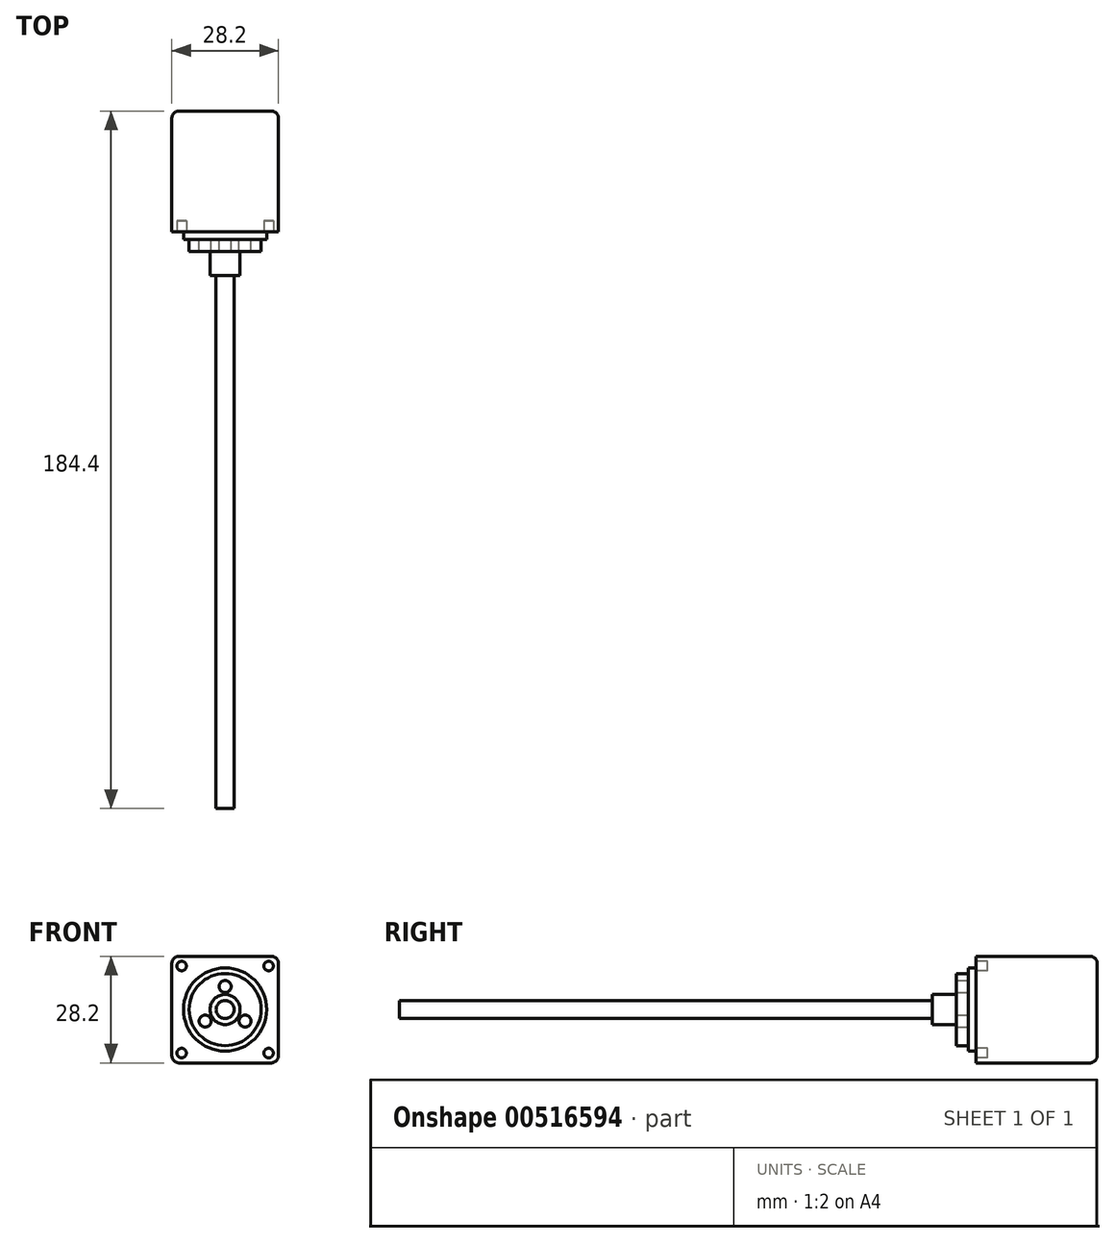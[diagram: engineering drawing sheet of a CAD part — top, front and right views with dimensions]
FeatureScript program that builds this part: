
annotation { "Feature Type Name" : "Feature", "Feature Type Description" : "" }
export const myFeature = defineFeature(function(context is Context, id is Id, definition is map)
    precondition{}
    {
        {
            var Q0;
            Q0=qCreatedBy(makeId("Front.planeOp"),FACE);
            var sketch = newSketch(context, id + "F0", { "sketchPlane" : qUnion([Q0])});
            skLineSegment(sketch, "E0.bottom", {"start": v(14.1, 14.1) * mm, "end": v(-14.1, 14.1) * mm});
            skLineSegment(sketch, "E0.top", {"start": v(14.1, -14.1) * mm, "end": v(-14.1, -14.1) * mm});
            skLineSegment(sketch, "E0.left", {"start": v(14.1, 14.1) * mm, "end": v(14.1, -14.1) * mm});
            skLineSegment(sketch, "E0.right", {"start": v(-14.1, 14.1) * mm, "end": v(-14.1, -14.1) * mm});
            skPoint(sketch, "E0.middle", {"position": v(0, 0) * mm});
            skCircle(sketch, "E1", {"center": v(0, 0) * mm, "radius": 11 * mm});
            skLineSegment(sketch, "E2.bottom", {"start": v(11.5, -11.5) * mm, "end": v(-11.5, -11.5) * mm, "construction": true});
            skLineSegment(sketch, "E2.top", {"start": v(11.5, 11.5) * mm, "end": v(-11.5, 11.5) * mm, "construction": true});
            skLineSegment(sketch, "E2.left", {"start": v(11.5, -11.5) * mm, "end": v(11.5, 11.5) * mm, "construction": true});
            skLineSegment(sketch, "E2.right", {"start": v(-11.5, -11.5) * mm, "end": v(-11.5, 11.5) * mm, "construction": true});
            skCircle(sketch, "E3", {"center": v(-11.5, 11.5) * mm, "radius": 1.25 * mm});
            skCircle(sketch, "E4", {"center": v(11.5, 11.5) * mm, "radius": 1.25 * mm});
            skCircle(sketch, "E5", {"center": v(-11.5, -11.5) * mm, "radius": 1.25 * mm});
            skCircle(sketch, "E6", {"center": v(11.5, -11.5) * mm, "radius": 1.25 * mm});
            skCircle(sketch, "E7", {"center": v(0, 0) * mm, "radius": 2.38 * mm});
            skSolve(sketch);
        }
        {
            var Q0;
            Q0=makeQuery(id+"F0.imprint","IMPRINT",FACE,{"disambiguationData":[TD([[makeQuery(id+"F0.imprint","IMPRINT",EDGE,{"derivedFrom":sQuery(id+"F0.wireOp",EDGE,"E0.bottom")}),1.0]])]});
            var Q1;
            Q1=makeQuery(id+"F0.imprint","IMPRINT",FACE,{"disambiguationData":[TD([[makeQuery(id+"F0.imprint","IMPRINT",EDGE,{"derivedFrom":sQuery(id+"F0.wireOp",EDGE,"E4")}),1.0]])]});
            var Q2;
            Q2=makeQuery(id+"F0.imprint","IMPRINT",FACE,{"disambiguationData":[TD([[makeQuery(id+"F0.imprint","IMPRINT",EDGE,{"derivedFrom":sQuery(id+"F0.wireOp",EDGE,"E6")}),1.0]])]});
            var Q3;
            Q3=makeQuery(id+"F0.imprint","IMPRINT",FACE,{"disambiguationData":[TD([[makeQuery(id+"F0.imprint","IMPRINT",EDGE,{"derivedFrom":sQuery(id+"F0.wireOp",EDGE,"E5")}),1.0]])]});
            var Q4;
            Q4=makeQuery(id+"F0.imprint","IMPRINT",FACE,{"disambiguationData":[TD([[makeQuery(id+"F0.imprint","IMPRINT",EDGE,{"derivedFrom":sQuery(id+"F0.wireOp",EDGE,"E3")}),1.0]])]});
            var Q5;
            Q5=makeQuery(id+"F0.imprint","IMPRINT",FACE,{"disambiguationData":[TD([[makeQuery(id+"F0.imprint","IMPRINT",EDGE,{"derivedFrom":sQuery(id+"F0.wireOp",EDGE,"E1")}),1.0]])]});
            var Q6;
            Q6=makeQuery(id+"F0.imprint","IMPRINT",FACE,{"disambiguationData":[TD([[makeQuery(id+"F0.imprint","IMPRINT",EDGE,{"derivedFrom":sQuery(id+"F0.wireOp",EDGE,"E7")}),1.0]])]});
            extrude(context, id + "F1", {"entities" : qUnion([Q0, Q1, Q2, Q3, Q4, Q5, Q6]), "oppositeDirection" : true, "depth" : 32 * mm, "offsetDistance" : 25 * mm});
        }
        {
            var Q0;
            Q0=makeQuery(id+"F0.imprint","IMPRINT",FACE,{"disambiguationData":[TD([[makeQuery(id+"F0.imprint","IMPRINT",EDGE,{"derivedFrom":sQuery(id+"F0.wireOp",EDGE,"E7")}),1.0]])]});
            extrude(context, id + "F2", {"entities" : qUnion([Q0]), "depth" : 152.4 * mm, "offsetDistance" : 25 * mm});
        }
        {
            var Q0;
            Q0=makeQuery(id+"F0.imprint","IMPRINT",FACE,{"disambiguationData":[TD([[makeQuery(id+"F0.imprint","IMPRINT",EDGE,{"derivedFrom":sQuery(id+"F0.wireOp",EDGE,"E1")}),1.0]])]});
            extrude(context, id + "F3", {"entities" : qUnion([Q0]), "operationType" : NewBodyOperationType.ADD, "depth" : 2 * mm, "offsetDistance" : 25 * mm});
        }
        {
            var Q0;
            Q0=makeQuery(id+"F0.imprint","IMPRINT",FACE,{"disambiguationData":[TD([[makeQuery(id+"F0.imprint","IMPRINT",EDGE,{"derivedFrom":sQuery(id+"F0.wireOp",EDGE,"E3")}),1.0]])]});
            var Q1;
            Q1=makeQuery(id+"F0.imprint","IMPRINT",FACE,{"disambiguationData":[TD([[makeQuery(id+"F0.imprint","IMPRINT",EDGE,{"derivedFrom":sQuery(id+"F0.wireOp",EDGE,"E4")}),1.0]])]});
            var Q2;
            Q2=makeQuery(id+"F0.imprint","IMPRINT",FACE,{"disambiguationData":[TD([[makeQuery(id+"F0.imprint","IMPRINT",EDGE,{"derivedFrom":sQuery(id+"F0.wireOp",EDGE,"E6")}),1.0]])]});
            var Q3;
            Q3=makeQuery(id+"F0.imprint","IMPRINT",FACE,{"disambiguationData":[TD([[makeQuery(id+"F0.imprint","IMPRINT",EDGE,{"derivedFrom":sQuery(id+"F0.wireOp",EDGE,"E5")}),1.0]])]});
            extrude(context, id + "F4", {"entities" : qUnion([Q0, Q1, Q2, Q3]), "operationType" : NewBodyOperationType.REMOVE, "oppositeDirection" : true, "depth" : 3 * mm, "offsetDistance" : 25 * mm});
        }
        {
            var Q0;
            Q0=makeQuery(id+"F1.opExtrude","SWEPT_EDGE",EDGE,{"disambiguationData":[OSD([sQuery(id+"F0.wireOp",EDGE,"E0.bottom"),sQuery(id+"F0.wireOp",EDGE,"E0.right")])]});
            var Q1;
            Q1=makeQuery(id+"F1.opExtrude","CAP_EDGE",EDGE,{"disambiguationData":[OSD([sQuery(id+"F0.wireOp",EDGE,"E0.bottom")])],"isStart":false});
            var Q2;
            Q2=makeQuery(id+"F1.opExtrude","SWEPT_EDGE",EDGE,{"disambiguationData":[OSD([sQuery(id+"F0.wireOp",EDGE,"E0.bottom"),sQuery(id+"F0.wireOp",EDGE,"E0.left")])]});
            var Q3;
            Q3=makeQuery(id+"F1.opExtrude","CAP_EDGE",EDGE,{"disambiguationData":[OSD([sQuery(id+"F0.wireOp",EDGE,"E0.left")])],"isStart":false});
            var Q4;
            Q4=makeQuery(id+"F1.opExtrude","SWEPT_EDGE",EDGE,{"disambiguationData":[OSD([sQuery(id+"F0.wireOp",EDGE,"E0.top"),sQuery(id+"F0.wireOp",EDGE,"E0.left")])]});
            var Q5;
            Q5=makeQuery(id+"F1.opExtrude","CAP_EDGE",EDGE,{"disambiguationData":[OSD([sQuery(id+"F0.wireOp",EDGE,"E0.top")])],"isStart":false});
            var Q6;
            Q6=makeQuery(id+"F1.opExtrude","SWEPT_EDGE",EDGE,{"disambiguationData":[OSD([sQuery(id+"F0.wireOp",EDGE,"E0.top"),sQuery(id+"F0.wireOp",EDGE,"E0.right")])]});
            var Q7;
            Q7=makeQuery(id+"F1.opExtrude","CAP_EDGE",EDGE,{"disambiguationData":[OSD([sQuery(id+"F0.wireOp",EDGE,"E0.right")])],"isStart":false});
            fillet(context, id + "F5", {"entities" : qUnion([Q0, Q1, Q2, Q3, Q4, Q5, Q6, Q7]), "radius" : 2 * mm, "tangentPropagation" : true, "allowEdgeOverflow" : false});
        }
        {
            var Q0;
            Q0=makeQuery(id+"F3.opExtrude","CAP_FACE",FACE,{"disambiguationData":[OSD([sQuery(id+"F0.wireOp",EDGE,"E1"),sQuery(id+"F0.wireOp",EDGE,"E7")])],"isStart":false});
            var sketch = newSketch(context, id + "F6", { "sketchPlane" : qUnion([Q0])});
            skCircle(sketch, "E8", {"center": v(0, 0) * mm, "radius": 9.53 * mm});
            skCircle(sketch, "E9", {"center": v(0, 0) * mm, "radius": 6.1 * mm, "construction": true});
            skCircle(sketch, "E10", {"center": v(0, 6.1) * mm, "radius": 1.59 * mm});
            skCircle(sketch, "E11", {"center": v(0, 0) * mm, "radius": 3.97 * mm});
            skCircle(sketch, "E12.1.0", {"center": v(-5.27, -3.04) * mm, "radius": 1.59 * mm});
            skCircle(sketch, "E12.2.0", {"center": v(5.27, -3.04) * mm, "radius": 1.59 * mm});
            skSolve(sketch);
        }
        {
            var Q0;
            Q0=makeQuery(id+"F6.imprint","IMPRINT",FACE,{"disambiguationData":[TD([[makeQuery(id+"F6.imprint","IMPRINT",EDGE,{"derivedFrom":sQuery(id+"F6.wireOp",EDGE,"E11")}),1.0]])]});
            extrude(context, id + "F7", {"entities" : qUnion([Q0]), "depth" : 9.53 * mm, "offsetDistance" : 25 * mm});
        }
        {
            var Q0;
            Q0=makeQuery(id+"F6.imprint","IMPRINT",FACE,{"disambiguationData":[TD([[makeQuery(id+"F6.imprint","IMPRINT",EDGE,{"derivedFrom":sQuery(id+"F6.wireOp",EDGE,"E8")}),1.0]])]});
            extrude(context, id + "F8", {"entities" : qUnion([Q0]), "operationType" : NewBodyOperationType.ADD, "depth" : 3.18 * mm, "offsetDistance" : 25 * mm});
        }
    });
